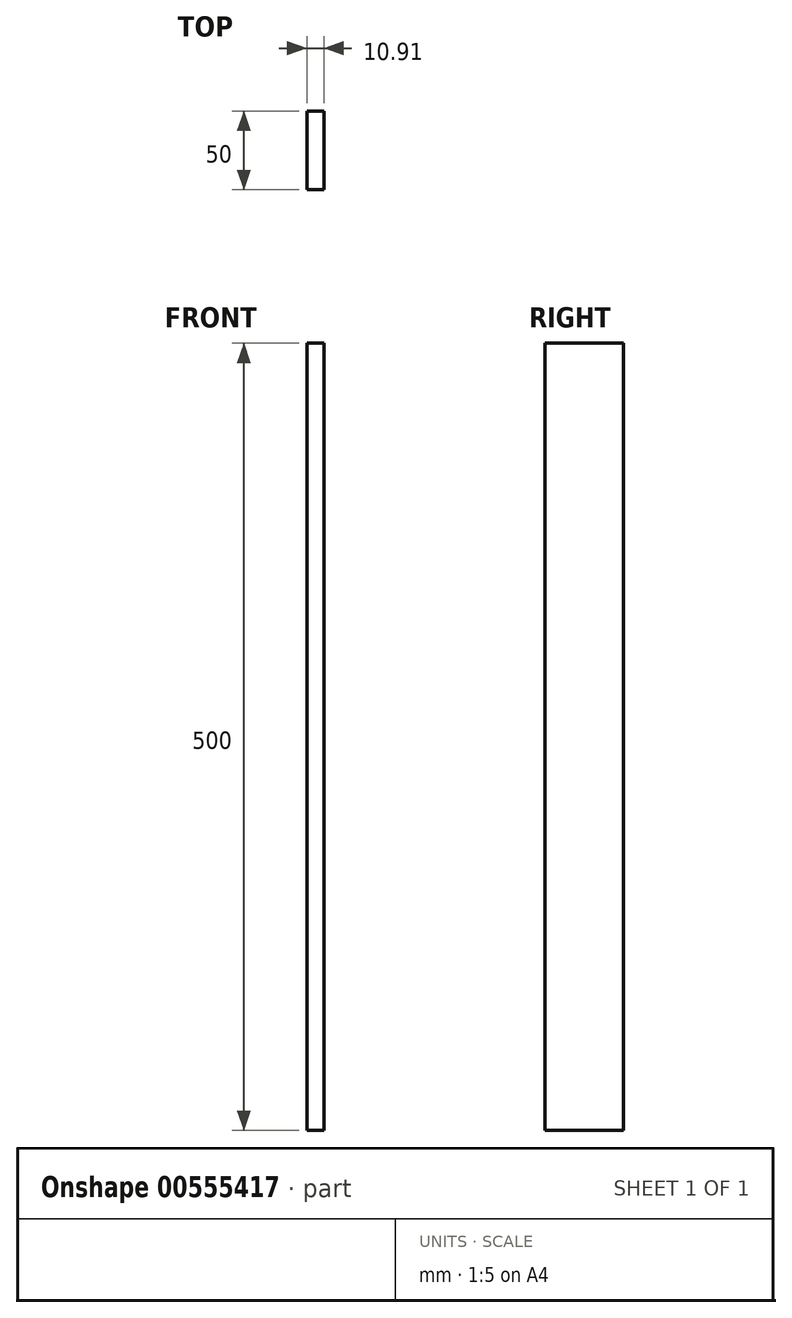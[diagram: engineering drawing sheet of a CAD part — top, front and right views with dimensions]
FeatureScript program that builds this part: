
annotation { "Feature Type Name" : "Feature", "Feature Type Description" : "" }
export const myFeature = defineFeature(function(context is Context, id is Id, definition is map)
    precondition{}
    {
        {
            var Q0;
            Q0=qCreatedBy(makeId("Front.planeOp"),FACE);
            var sketch = newSketch(context, id + "F0", { "sketchPlane" : qUnion([Q0])});
            skLineSegment(sketch, "E0.bottom", {"start": v(0, 74.5) * mm, "end": v(-10.9, 74.5) * mm});
            skLineSegment(sketch, "E0.top", {"start": v(0, -425.5) * mm, "end": v(-10.9, -425.5) * mm});
            skLineSegment(sketch, "E0.left", {"start": v(0, 74.5) * mm, "end": v(0, -425.5) * mm});
            skLineSegment(sketch, "E0.right", {"start": v(-10.9, 74.5) * mm, "end": v(-10.9, -425.5) * mm});
            skSolve(sketch);
        }
        {
            var Q0;
            Q0=makeQuery(id+"F0.imprint","IMPRINT",FACE,{"disambiguationData":[TD([[makeQuery(id+"F0.imprint","IMPRINT",EDGE,{"derivedFrom":sQuery(id+"F0.wireOp",EDGE,"E0.bottom")}),1.0]])]});
            extrude(context, id + "F1", {"entities" : qUnion([Q0]), "depth" : 50 * mm, "offsetDistance" : 25 * mm});
        }
    });
